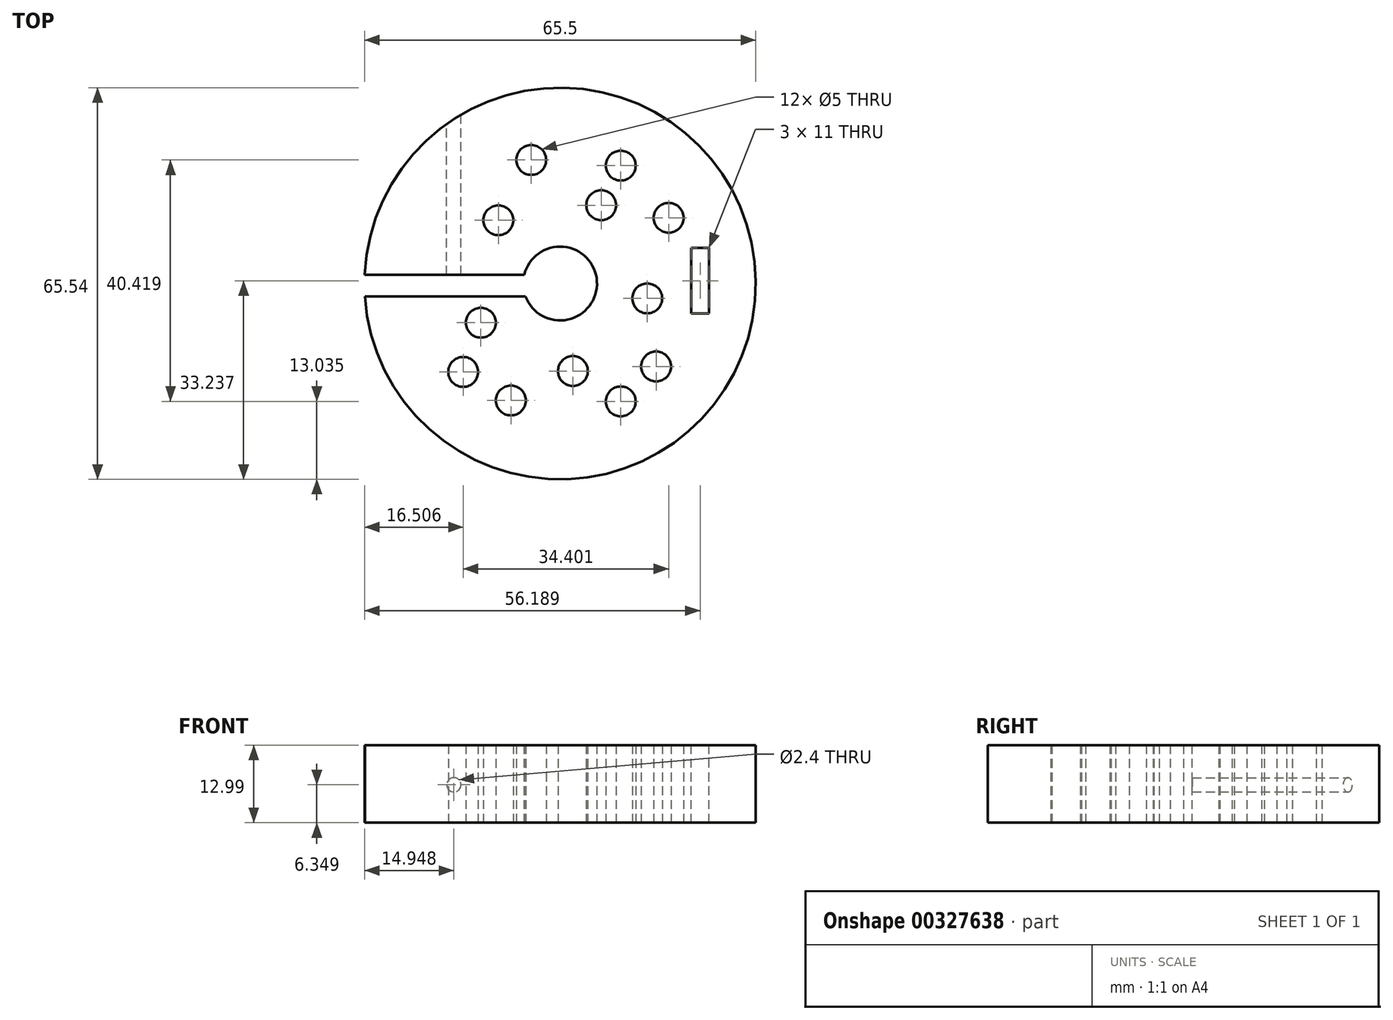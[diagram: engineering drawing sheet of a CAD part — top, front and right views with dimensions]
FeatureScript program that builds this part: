
annotation { "Feature Type Name" : "Feature", "Feature Type Description" : "" }
export const myFeature = defineFeature(function(context is Context, id is Id, definition is map)
    precondition{}
    {
        {
            var Q0;
            Q0=qCreatedBy(makeId("Front.planeOp"),FACE);
            var sketch = newSketch(context, id + "F0", { "sketchPlane" : qUnion([Q0])});
            skLineSegment(sketch, "E0", {"start": v(6.17, 0) * mm, "end": v(6.17, 13) * mm});
            skLineSegment(sketch, "E1", {"start": v(6.17, 13) * mm, "end": v(32.77, 13) * mm});
            skLineSegment(sketch, "E2", {"start": v(32.77, 13) * mm, "end": v(32.77, 0) * mm});
            skLineSegment(sketch, "E3", {"start": v(32.77, 0) * mm, "end": v(6.17, 0) * mm});
            skLineSegment(sketch, "E4", {"start": v(0, 36.43) * mm, "end": v(0, -20.3) * mm, "construction": true});
            skSolve(sketch);
        }
        {
            var Q0;
            Q0=makeQuery(id+"F0.imprint","IMPRINT",FACE,{"disambiguationData":[TD([[makeQuery(id+"F0.imprint","IMPRINT",EDGE,{"derivedFrom":sQuery(id+"F0.wireOp",EDGE,"E0")}),-1.0]])]});
            var Q1;
            Q1=sQuery(id+"F0.wireOp",EDGE,"E4");
            revolve(context, id + "F1", {"entities" : qUnion([Q0]), "axis" : qUnion([Q1]), "revolveType" : RevolveType.FULL});
        }
        {
            var Q0;
            Q0=makeQuery(id+"F1.opRevolve","SWEPT_FACE",FACE,{"disambiguationData":[OSD([sQuery(id+"F0.wireOp",EDGE,"E1")])]});
            var sketch = newSketch(context, id + "F2", { "sketchPlane" : qUnion([Q0])});
            skLineSegment(sketch, "E5", {"start": v(-6, 1.45) * mm, "end": v(-35.7, 1.45) * mm});
            skLineSegment(sketch, "E6", {"start": v(-35.7, 1.45) * mm, "end": v(-35.7, -2.15) * mm});
            skLineSegment(sketch, "E7", {"start": v(-35.7, -2.15) * mm, "end": v(-5.79, -2.15) * mm});
            skLineSegment(sketch, "E8", {"start": v(-5.79, -2.15) * mm, "end": v(-6, 1.45) * mm});
            skLineSegment(sketch, "E9.bottom", {"start": v(21.96, -5.03) * mm, "end": v(24.96, -5.03) * mm});
            skLineSegment(sketch, "E9.top", {"start": v(21.96, 5.97) * mm, "end": v(24.96, 5.97) * mm});
            skLineSegment(sketch, "E9.left", {"start": v(21.96, -5.03) * mm, "end": v(21.96, 5.97) * mm});
            skLineSegment(sketch, "E9.right", {"start": v(24.96, -5.03) * mm, "end": v(24.96, 5.97) * mm});
            skSolve(sketch);
        }
        {
            var Q0;
            Q0 = qSketchRegion(id + "F2", true);
            extrude(context, id + "F3", {"entities" : qUnion([Q0]), "operationType" : NewBodyOperationType.REMOVE, "oppositeDirection" : true, "depth" : 25 * mm});
        }
        {
            var Q0;
            Q0=makeQuery(id+"F1.opRevolve","SWEPT_FACE",FACE,{"disambiguationData":[OSD([sQuery(id+"F0.wireOp",EDGE,"E1")])]});
            var sketch = newSketch(context, id + "F4", { "sketchPlane" : qUnion([Q0])});
            skPoint(sketch, "E10", {"position": v(-10.34, 10.6) * mm});
            skPoint(sketch, "E11.1.0", {"position": v(-13.27, -6.56) * mm});
            skPoint(sketch, "E11.2.0", {"position": v(2.14, -14.65) * mm});
            skPoint(sketch, "E11.3.0", {"position": v(14.59, -2.5) * mm});
            skPoint(sketch, "E11.4.0", {"position": v(6.88, 13.1) * mm});
            skPoint(sketch, "E11.center", {"position": v(0, 0) * mm});
            skPoint(sketch, "E12", {"position": v(-4.84, 20.68) * mm});
            skPoint(sketch, "E13.1.0", {"position": v(-21.17, 1.79) * mm});
            skPoint(sketch, "E13.2.0", {"position": v(-8.24, -19.58) * mm});
            skPoint(sketch, "E13.3.0", {"position": v(16.07, -13.89) * mm});
            skPoint(sketch, "E13.4.0", {"position": v(18.18, 11) * mm});
            skPoint(sketch, "E14", {"position": v(-21.35, 11.95) * mm});
            skPoint(sketch, "E15", {"position": v(-16.22, -14.8) * mm});
            skPoint(sketch, "E16", {"position": v(10.15, 19.73) * mm});
            skPoint(sketch, "E17", {"position": v(10.15, -19.73) * mm});
            skSolve(sketch);
        }
        {
            var Q0;
            Q0=sQuery(id+"F4.wireOp",VERTEX,"E10");
            var Q1;
            Q1=sQuery(id+"F4.wireOp",VERTEX,"E11.4.0");
            var Q2;
            Q2=sQuery(id+"F4.wireOp",VERTEX,"E11.3.0");
            var Q3;
            Q3=sQuery(id+"F4.wireOp",VERTEX,"E11.2.0");
            var Q4;
            Q4=sQuery(id+"F4.wireOp",VERTEX,"E11.1.0");
            var Q5;
            Q5=sQuery(id+"F4.wireOp",VERTEX,"E12");
            var Q6;
            Q6=sQuery(id+"F4.wireOp",VERTEX,"E13.4.0");
            var Q7;
            Q7=sQuery(id+"F4.wireOp",VERTEX,"E13.2.0");
            var Q8;
            Q8=sQuery(id+"F4.wireOp",VERTEX,"E13.3.0");
            var Q9;
            Q9=sQuery(id+"F4.wireOp",VERTEX,"E16");
            var Q10;
            Q10=sQuery(id+"F4.wireOp",VERTEX,"E17");
            var Q11;
            Q11=sQuery(id+"F4.wireOp",VERTEX,"E15");
            var Q12;
            Q12=makeQuery(id+"F1.opRevolve","SWEPT_BODY",BODY,{"disambiguationData":[OSD([sQuery(id+"F0.wireOp",EDGE,"E0"),sQuery(id+"F0.wireOp",EDGE,"E1"),sQuery(id+"F0.wireOp",EDGE,"E2"),sQuery(id+"F0.wireOp",EDGE,"E3")])]});
            hole(context, id + "F5", {"style" : HoleStyle.SIMPLE, "endStyle" : HoleEndStyle.THROUGH, "standardTappedOrClearance" : lookupTablePath({ "standard" : "ISO", "engagement" : "75%", "pitch" : "1 mm", "size" : "M6", "type" : "Tapped" }), "standardBlindInLast" : lookupTablePath({ "standard" : "ISO", "engagement" : "75%", "pitch" : "1 mm", "size" : "M6", "type" : "Tapped" }), "holeDiameter" : 5 * mm, "showTappedDepth" : true, "isTappedThrough" : true, "tappedDepth" : 12 * mm, "tapClearance" : 3, "startFromSketch" : true, "locations" : qUnion([Q0, Q1, Q2, Q3, Q4, Q5, Q6, Q7, Q8, Q9, Q10, Q11]), "scope" : qUnion([Q12]), "majorDiameter" : 6 * mm});
        }
        {
            var Q0;
            Q0=qCreatedBy(makeId("Front.planeOp"),FACE);
            var sketch = newSketch(context, id + "F6", { "sketchPlane" : qUnion([Q0])});
            skPoint(sketch, "E18", {"position": v(-17.78, 6.35) * mm});
            skSolve(sketch);
        }
        {
            var Q0;
            Q0=sQuery(id+"F6.wireOp",VERTEX,"E18");
            var Q1;
            Q1=makeQuery(id+"F1.opRevolve","SWEPT_BODY",BODY,{"disambiguationData":[OSD([sQuery(id+"F0.wireOp",EDGE,"E0"),sQuery(id+"F0.wireOp",EDGE,"E1"),sQuery(id+"F0.wireOp",EDGE,"E2"),sQuery(id+"F0.wireOp",EDGE,"E3")])]});
            hole(context, id + "F7", {"style" : HoleStyle.SIMPLE, "endStyle" : HoleEndStyle.THROUGH, "standardTappedOrClearance" : lookupTablePath({ "standard" : "ISO", "engagement" : "75%", "pitch" : "0.6 mm", "size" : "M3", "type" : "Tapped" }), "standardBlindInLast" : lookupTablePath({ "standard" : "ISO", "engagement" : "75%", "pitch" : "0.6 mm", "size" : "M3", "type" : "Tapped" }), "holeDiameter" : 2.4 * mm, "showTappedDepth" : true, "isTappedThrough" : true, "tappedDepth" : 12 * mm, "tapClearance" : 3, "startFromSketch" : true, "locations" : qUnion([Q0]), "scope" : qUnion([Q1])});
        }
    });
